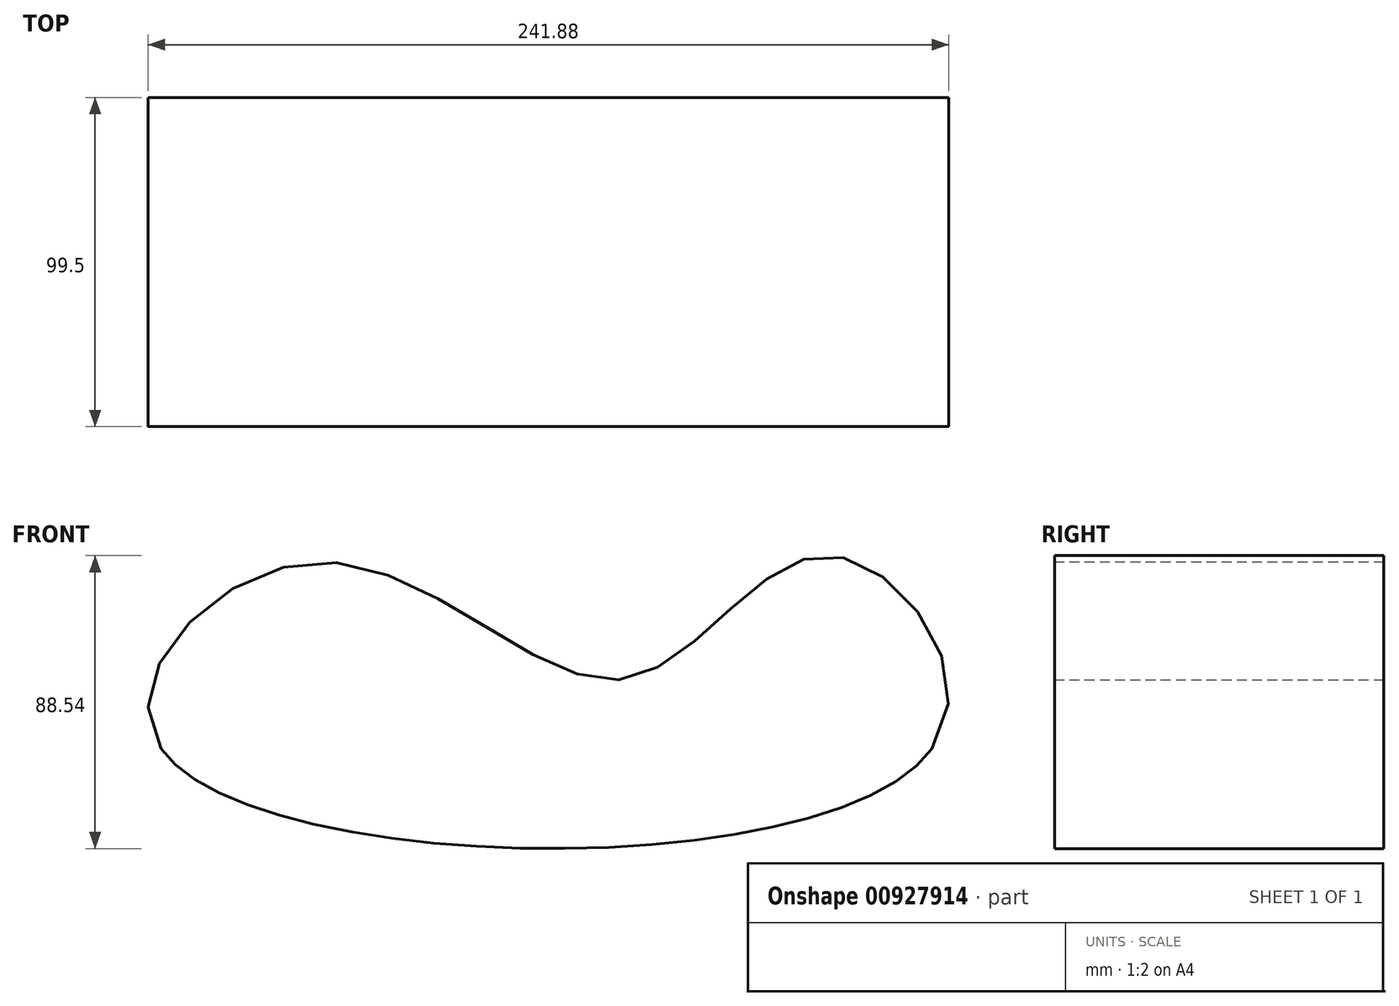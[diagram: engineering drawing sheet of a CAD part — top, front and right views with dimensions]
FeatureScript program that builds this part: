
annotation { "Feature Type Name" : "Feature", "Feature Type Description" : "" }
export const myFeature = defineFeature(function(context is Context, id is Id, definition is map)
    precondition{}
    {
        {
            var Q0;
            Q0=qCreatedBy(makeId("Front.planeOp"),FACE);
            var sketch = newSketch(context, id + "F0", { "sketchPlane" : qUnion([Q0])});
            skFitSpline(sketch, "E0", {"points": [v(-110.98, 0) * mm, v(-64.7, 56.33) * mm, v(28.69, 20.91) * mm, v(91.45, 58.29) * mm, v(121.97, 0) * mm, v(-110.98, 0) * mm]});
            skLineSegment(sketch, "E1", {"start": v(121.97, 0) * mm, "end": v(-110.98, 0) * mm});
            skSolve(sketch);
        }
        {
            var Q0;
            Q0=makeQuery(id+"F0.imprint","IMPRINT",FACE,{"disambiguationData":[TD([[makeQuery(id+"F0.imprint","IMPRINT",EDGE,{"derivedFrom":sQuery(id+"F0.wireOp",EDGE,"E0")}),-1.0]])]});
            extrude(context, id + "F1", {"entities" : qUnion([Q0]), "oppositeDirection" : true, "depth" : 99.5 * mm, "offsetDistance" : 25.4 * mm});
        }
    });
